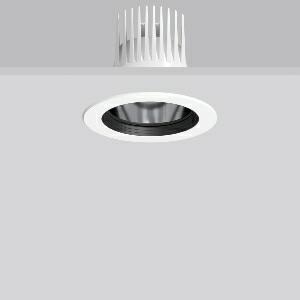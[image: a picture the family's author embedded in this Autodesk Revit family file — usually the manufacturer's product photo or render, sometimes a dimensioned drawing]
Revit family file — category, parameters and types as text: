
# Revit family: heledon_maxi_e_901763_002_ebf0
name_source: partatom
category: Lighting Fixtures
units: mm (PartAtom-declared; Revit-internal decimal feet)

## family parameters
Cut with Voids When Loaded = No
Host = Face
Light Source = No
Part Type = Normal
Room Calculation Point = No
Round Connector Dimension = Use Diameter
Shared = No

## types (1)
- HELEDON maxi E (1 x LED Modul 930, 4200 lm, 3000)
    Apparent Load = 35 VA
    Approval mark = CE
    CIE Flux Codes = 100 100 100 100 100
    Color Rendering = 90
    Color Temperature = 3000
    Default Elevation = 1800 mm
    Description = Series: HELEDON maxi
Round recessed downlight. Housing: die-cast aluminium, powder-coated. Black plastic ring and recessed LED to prevent glare from the side. Optical assembly with reflector made of MIRO-Silver with 98% total light reflection for outstanding efficiency - can be changed without tools. Best colour rendering index Ra>90. Suitable for Recessed ceiling mounting. Installation without tools thanks to spring fastening system. Including separate LED converter with connecting cable 600 mm.High quality converter without flickering and stroboscopic effect. Through-wiring box (5 pole) available as accessory. The following accessories can be mounted without use of tools: interchangeable lenses, decorative glasses, honeycomb louvre, clear and frosted diffusers, white interchangeable plastic ring. 
Colour: traffic white, matt (RAL 9016)
Diameter: 162 mm
Height: 3 mm
Cut-out diameter: 152 mm
Recess height: 200 mm
Luminaire: recess height: 135 mm
Lamp: LED
Socket: without socket
Colour temperature: 3000K
Colour rendering index (CRI): 92
System power: 35 W
Rated luminous flux: 4200 lm
Luminous efficiency: 120 lm/W
Control gear: Regulated power supply
Protection class: II
Type of protection: IP 20
    Height = 0 mm  [stored 0 ft]
    Lamp = 1 x LED Modul 930
    Lamp Light Flux = 4200 lm
    Lamp count = 1
    Length = 162 mm
    Lifetime = 50000 h
    Luminous efficacy = 120 lm/W
    Manufacturer = RZB
    ModVariant = No
    Model = 901763.002
    Mounting Place = Ceiling
    Mounting Type = Recessed
    Number of Poles = 1
    OnlyDefault = Yes
    Power Factor = 1
    Product Name = HELEDON maxi E
    Product group = Recessed downlights
    ProductGroupID = 402
    Protection Class = Protection class II
    Protection Degree = IP 20
    RLX_Detail_Level = 1
    RLX_Emergency_Light_Flux = 0 lm
    RLX_Emergency_Type = 0
    RLX_Emergency_Type_DB = No
    RlxData = <blob elided: 118961 chars, md5=5f861109>
    Socket = socket
    Standby Power = 0 W
    System Light Flux = 4200 lm
    System Power = 35 W
    Type Comments = Product without accessories
    Type Image = 901662.002.jpg
    URL = http://relux.com
    VarID = ---
    Voltage = 230 V
    Voltage Range = 220-240 V
    Weight = 0.00 kg
    Width = 0 mm  [stored 0 ft]

note: [stored X ft] marks values corroborated as IEEE doubles in the binary element streams (Revit-internal decimal feet)

## geometry (parser evidence)
native form markers: Blend x4, Sweep x11
no freeform markers — native parametric forms only
